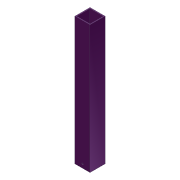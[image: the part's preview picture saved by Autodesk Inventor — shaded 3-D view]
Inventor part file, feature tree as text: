
AUTODESK INVENTOR PART (.ipt)
format: ipt  version: 2012 (Build 160160000, 160)  size: 82,944 bytes
history: native  units: in
note: dims shown in document units (in); Inventor stores cm internally (conversion verified against a paired STEP export)
features: extrude x2, sketch x2, shell x1
ambient origin geometry x8: Origin, YZ Plane, XZ Plane, XY Plane, X Axis, Y Axis, Z Axis, Center Point
bodies: Solid1 (feature_tree)
feature tree (5):
  extrude  "Extrusion1"  Depth=17.0in
  shell  "Shell1"  Thickness=2.0in
  extrude  "Extrusion3"  Depth=0.375in
  sketch  "Sketch1"  dims[d0=2.0in d1=17.0in d2=2.0in d3=0.0in]
  sketch  "Sketch3"  dims[d4=0.125in d10=0.375in d11=1.0in d12=0.25in d13=1.0in d14=0.0in]
